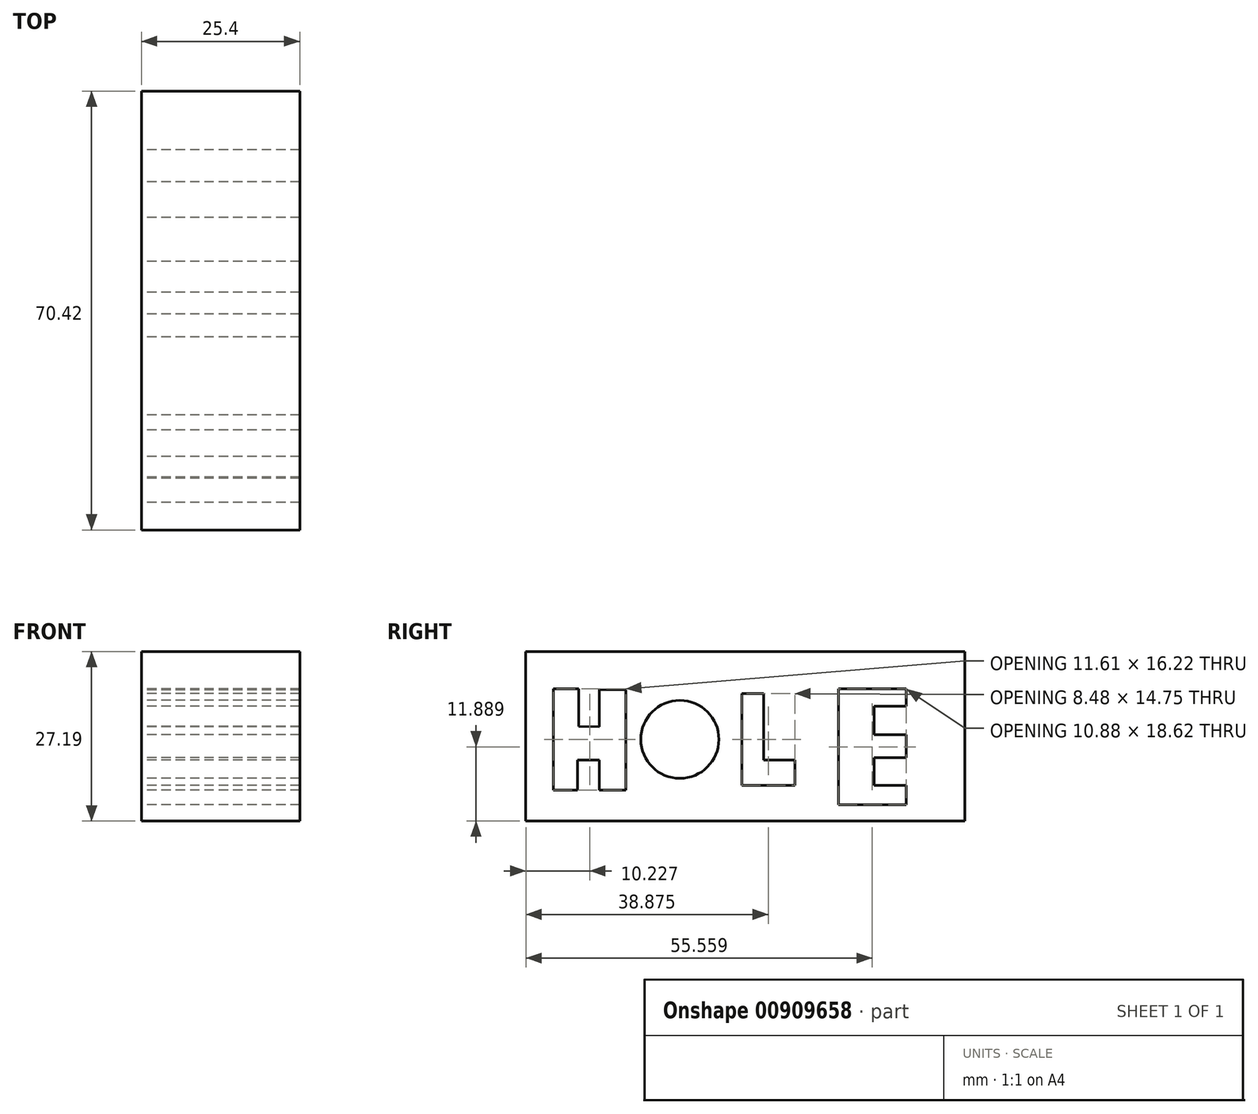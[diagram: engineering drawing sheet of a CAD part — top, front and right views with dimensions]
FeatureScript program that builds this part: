
annotation { "Feature Type Name" : "Feature", "Feature Type Description" : "" }
export const myFeature = defineFeature(function(context is Context, id is Id, definition is map)
    precondition{}
    {
        {
            var Q0;
            Q0=qCreatedBy(makeId("Right.planeOp"),FACE);
            var sketch = newSketch(context, id + "F0", { "sketchPlane" : qUnion([Q0])});
            skLineSegment(sketch, "E0", {"start": v(-26.45, 0) * mm, "end": v(-26.45, -27.2) * mm});
            skLineSegment(sketch, "E1", {"start": v(-26.45, -27.2) * mm, "end": v(43.97, -27.2) * mm});
            skLineSegment(sketch, "E2", {"start": v(43.97, -27.2) * mm, "end": v(43.97, 0) * mm});
            skLineSegment(sketch, "E3", {"start": v(-26.45, 0) * mm, "end": v(43.97, 0) * mm});
            skSolve(sketch);
        }
        {
            var Q0;
            Q0 = qSketchRegion(id + "F0", true);
            extrude(context, id + "F1", {"entities" : qUnion([Q0]), "depth" : 25.4 * mm, "offsetDistance" : 25.4 * mm});
        }
        {
            var Q0;
            Q0=qCreatedBy(makeId("Right.planeOp"),FACE);
            var sketch = newSketch(context, id + "F2", { "sketchPlane" : qUnion([Q0])});
            skCircle(sketch, "E4", {"center": v(-1.75, -14.1) * mm, "radius": 6.26 * mm});
            skLineSegment(sketch, "E5", {"start": v(-22.03, -6) * mm, "end": v(-22.03, -22.21) * mm});
            skLineSegment(sketch, "E6", {"start": v(-22.03, -22.21) * mm, "end": v(-18.16, -22.21) * mm});
            skLineSegment(sketch, "E7", {"start": v(-18.16, -22.21) * mm, "end": v(-18.16, -17.42) * mm});
            skLineSegment(sketch, "E8", {"start": v(-18.16, -17.42) * mm, "end": v(-14.66, -17.42) * mm});
            skLineSegment(sketch, "E9", {"start": v(-14.66, -17.42) * mm, "end": v(-14.66, -22.21) * mm});
            skLineSegment(sketch, "E10", {"start": v(-14.66, -22.21) * mm, "end": v(-10.42, -22.21) * mm});
            skLineSegment(sketch, "E11", {"start": v(-10.42, -22.21) * mm, "end": v(-10.42, -6.18) * mm});
            skLineSegment(sketch, "E12", {"start": v(-14.66, -6.1) * mm, "end": v(-14.66, -12.08) * mm});
            skLineSegment(sketch, "E13", {"start": v(-14.66, -12.08) * mm, "end": v(-17.97, -12.02) * mm});
            skLineSegment(sketch, "E14", {"start": v(-17.97, -12.26) * mm, "end": v(-17.97, -6) * mm});
            skLineSegment(sketch, "E15", {"start": v(-17.97, -6) * mm, "end": v(-22.03, -6) * mm});
            skLineSegment(sketch, "E16", {"start": v(-14.66, -6.1) * mm, "end": v(-10.42, -6.18) * mm});
            skLineSegment(sketch, "E17", {"start": v(8.18, -6.73) * mm, "end": v(8.18, -21.48) * mm});
            skLineSegment(sketch, "E18", {"start": v(8.18, -21.48) * mm, "end": v(16.66, -21.48) * mm});
            skLineSegment(sketch, "E19", {"start": v(16.66, -21.48) * mm, "end": v(16.66, -17.42) * mm});
            skLineSegment(sketch, "E20", {"start": v(16.66, -17.42) * mm, "end": v(11.69, -17.42) * mm});
            skLineSegment(sketch, "E21", {"start": v(11.69, -17.42) * mm, "end": v(11.69, -6.73) * mm});
            skLineSegment(sketch, "E22", {"start": v(11.69, -6.73) * mm, "end": v(8.18, -6.73) * mm});
            skLineSegment(sketch, "E23", {"start": v(23.67, -6) * mm, "end": v(34.55, -6) * mm});
            skLineSegment(sketch, "E24", {"start": v(34.55, -6) * mm, "end": v(34.55, -8.76) * mm});
            skLineSegment(sketch, "E25", {"start": v(34.55, -8.76) * mm, "end": v(29.39, -8.76) * mm});
            skLineSegment(sketch, "E26", {"start": v(29.39, -8.76) * mm, "end": v(29.39, -13.37) * mm});
            skLineSegment(sketch, "E27", {"start": v(29.39, -13.37) * mm, "end": v(34.55, -13.37) * mm});
            skLineSegment(sketch, "E28", {"start": v(34.55, -13.37) * mm, "end": v(34.55, -17.05) * mm});
            skLineSegment(sketch, "E29", {"start": v(34.55, -17.05) * mm, "end": v(29.39, -17.05) * mm});
            skLineSegment(sketch, "E30", {"start": v(29.39, -17.05) * mm, "end": v(29.39, -21.48) * mm});
            skLineSegment(sketch, "E31", {"start": v(29.39, -21.48) * mm, "end": v(34.55, -21.48) * mm});
            skLineSegment(sketch, "E32", {"start": v(34.55, -21.48) * mm, "end": v(34.55, -24.61) * mm});
            skLineSegment(sketch, "E33", {"start": v(34.55, -24.61) * mm, "end": v(23.67, -24.61) * mm});
            skLineSegment(sketch, "E34", {"start": v(23.67, -24.61) * mm, "end": v(23.67, -6) * mm});
            skSolve(sketch);
        }
        {
            var Q0;
            Q0 = qSketchRegion(id + "F2", true);
            extrude(context, id + "F3", {"entities" : qUnion([Q0]), "operationType" : NewBodyOperationType.REMOVE, "depth" : 38.1 * mm, "offsetDistance" : 25.4 * mm});
        }
    });
